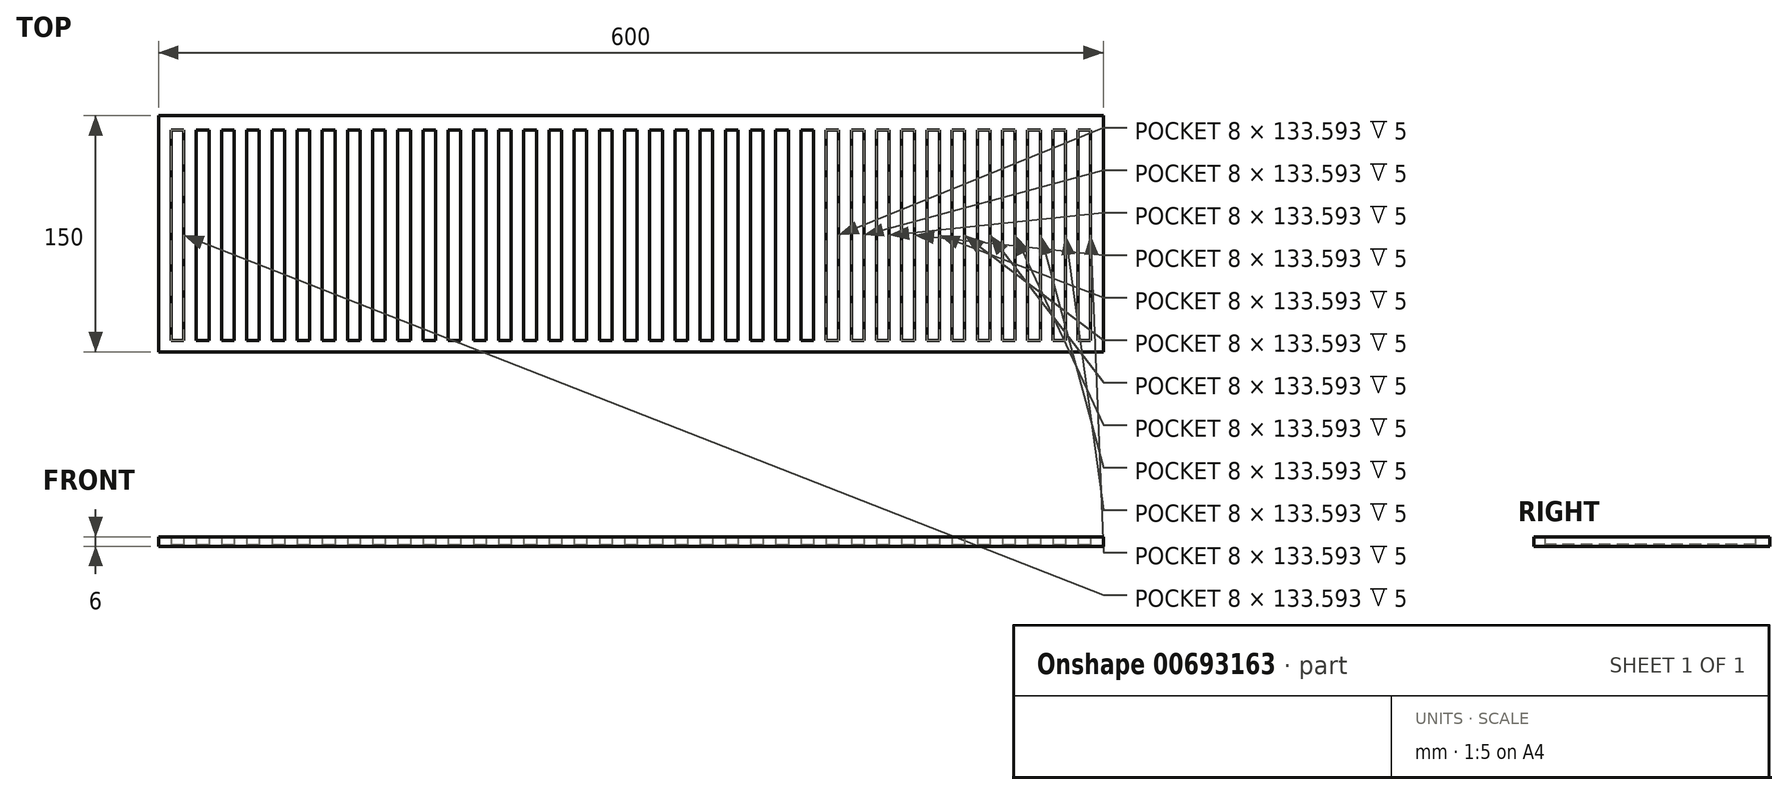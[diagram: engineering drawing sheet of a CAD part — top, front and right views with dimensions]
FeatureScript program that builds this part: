
annotation { "Feature Type Name" : "Feature", "Feature Type Description" : "" }
export const myFeature = defineFeature(function(context is Context, id is Id, definition is map)
    precondition{}
    {
        {
            var Q0;
            Q0=qCreatedBy(makeId("Top.planeOp"),FACE);
            var sketch = newSketch(context, id + "F0", { "sketchPlane" : qUnion([Q0])});
            skLineSegment(sketch, "E0.bottom", {"start": v(-288.8, 29.5) * mm, "end": v(311.2, 29.5) * mm});
            skLineSegment(sketch, "E0.top", {"start": v(-288.8, -120.5) * mm, "end": v(311.2, -120.5) * mm});
            skLineSegment(sketch, "E0.left", {"start": v(-288.8, 29.5) * mm, "end": v(-288.8, -120.5) * mm});
            skLineSegment(sketch, "E0.right", {"start": v(311.2, 29.5) * mm, "end": v(311.2, -120.5) * mm});
            skLineSegment(sketch, "E1.bottom", {"start": v(-280.8, 20.35) * mm, "end": v(-272.8, 20.35) * mm});
            skLineSegment(sketch, "E1.top", {"start": v(-280.8, -113.25) * mm, "end": v(-272.8, -113.25) * mm});
            skLineSegment(sketch, "E1.left", {"start": v(-280.8, 20.35) * mm, "end": v(-280.8, -113.25) * mm});
            skLineSegment(sketch, "E1.right", {"start": v(-272.8, 20.35) * mm, "end": v(-272.8, -113.25) * mm});
            skLineSegment(sketch, "E2.1.0.0", {"start": v(-264.8, 20.35) * mm, "end": v(-256.8, 20.35) * mm});
            skLineSegment(sketch, "E2.1.0.1", {"start": v(-264.8, 20.35) * mm, "end": v(-264.8, -113.25) * mm});
            skLineSegment(sketch, "E2.1.0.2", {"start": v(-256.8, 20.35) * mm, "end": v(-256.8, -113.25) * mm});
            skLineSegment(sketch, "E2.1.0.3", {"start": v(-264.8, -113.25) * mm, "end": v(-256.8, -113.25) * mm});
            skLineSegment(sketch, "E2.2.0.0", {"start": v(-248.8, 20.35) * mm, "end": v(-240.8, 20.35) * mm});
            skLineSegment(sketch, "E2.2.0.1", {"start": v(-248.8, 20.35) * mm, "end": v(-248.8, -113.25) * mm});
            skLineSegment(sketch, "E2.2.0.2", {"start": v(-240.8, 20.35) * mm, "end": v(-240.8, -113.25) * mm});
            skLineSegment(sketch, "E2.2.0.3", {"start": v(-248.8, -113.25) * mm, "end": v(-240.8, -113.25) * mm});
            skLineSegment(sketch, "E2.3.0.0", {"start": v(-232.8, 20.35) * mm, "end": v(-224.8, 20.35) * mm});
            skLineSegment(sketch, "E2.3.0.1", {"start": v(-232.8, 20.35) * mm, "end": v(-232.8, -113.25) * mm});
            skLineSegment(sketch, "E2.3.0.2", {"start": v(-224.8, 20.35) * mm, "end": v(-224.8, -113.25) * mm});
            skLineSegment(sketch, "E2.3.0.3", {"start": v(-232.8, -113.25) * mm, "end": v(-224.8, -113.25) * mm});
            skLineSegment(sketch, "E2.4.0.0", {"start": v(-216.8, 20.35) * mm, "end": v(-208.8, 20.35) * mm});
            skLineSegment(sketch, "E2.4.0.1", {"start": v(-216.8, 20.35) * mm, "end": v(-216.8, -113.25) * mm});
            skLineSegment(sketch, "E2.4.0.2", {"start": v(-208.8, 20.35) * mm, "end": v(-208.8, -113.25) * mm});
            skLineSegment(sketch, "E2.4.0.3", {"start": v(-216.8, -113.25) * mm, "end": v(-208.8, -113.25) * mm});
            skLineSegment(sketch, "E2.5.0.0", {"start": v(-200.8, 20.35) * mm, "end": v(-192.8, 20.35) * mm});
            skLineSegment(sketch, "E2.5.0.1", {"start": v(-200.8, 20.35) * mm, "end": v(-200.8, -113.25) * mm});
            skLineSegment(sketch, "E2.5.0.2", {"start": v(-192.8, 20.35) * mm, "end": v(-192.8, -113.25) * mm});
            skLineSegment(sketch, "E2.5.0.3", {"start": v(-200.8, -113.25) * mm, "end": v(-192.8, -113.25) * mm});
            skLineSegment(sketch, "E2.6.0.0", {"start": v(-184.8, 20.35) * mm, "end": v(-176.8, 20.35) * mm});
            skLineSegment(sketch, "E2.6.0.1", {"start": v(-184.8, 20.35) * mm, "end": v(-184.8, -113.25) * mm});
            skLineSegment(sketch, "E2.6.0.2", {"start": v(-176.8, 20.35) * mm, "end": v(-176.8, -113.25) * mm});
            skLineSegment(sketch, "E2.6.0.3", {"start": v(-184.8, -113.25) * mm, "end": v(-176.8, -113.25) * mm});
            skLineSegment(sketch, "E2.7.0.0", {"start": v(-168.8, 20.35) * mm, "end": v(-160.8, 20.35) * mm});
            skLineSegment(sketch, "E2.7.0.1", {"start": v(-168.8, 20.35) * mm, "end": v(-168.8, -113.25) * mm});
            skLineSegment(sketch, "E2.7.0.2", {"start": v(-160.8, 20.35) * mm, "end": v(-160.8, -113.25) * mm});
            skLineSegment(sketch, "E2.7.0.3", {"start": v(-168.8, -113.25) * mm, "end": v(-160.8, -113.25) * mm});
            skLineSegment(sketch, "E2.8.0.0", {"start": v(-152.8, 20.35) * mm, "end": v(-144.8, 20.35) * mm});
            skLineSegment(sketch, "E2.8.0.1", {"start": v(-152.8, 20.35) * mm, "end": v(-152.8, -113.25) * mm});
            skLineSegment(sketch, "E2.8.0.2", {"start": v(-144.8, 20.35) * mm, "end": v(-144.8, -113.25) * mm});
            skLineSegment(sketch, "E2.8.0.3", {"start": v(-152.8, -113.25) * mm, "end": v(-144.8, -113.25) * mm});
            skLineSegment(sketch, "E2.9.0.0", {"start": v(-136.8, 20.35) * mm, "end": v(-128.8, 20.35) * mm});
            skLineSegment(sketch, "E2.9.0.1", {"start": v(-136.8, 20.35) * mm, "end": v(-136.8, -113.25) * mm});
            skLineSegment(sketch, "E2.9.0.2", {"start": v(-128.8, 20.35) * mm, "end": v(-128.8, -113.25) * mm});
            skLineSegment(sketch, "E2.9.0.3", {"start": v(-136.8, -113.25) * mm, "end": v(-128.8, -113.25) * mm});
            skLineSegment(sketch, "E2.10.0.0", {"start": v(-120.8, 20.35) * mm, "end": v(-112.8, 20.35) * mm});
            skLineSegment(sketch, "E2.10.0.1", {"start": v(-120.8, 20.35) * mm, "end": v(-120.8, -113.25) * mm});
            skLineSegment(sketch, "E2.10.0.2", {"start": v(-112.8, 20.35) * mm, "end": v(-112.8, -113.25) * mm});
            skLineSegment(sketch, "E2.10.0.3", {"start": v(-120.8, -113.25) * mm, "end": v(-112.8, -113.25) * mm});
            skLineSegment(sketch, "E2.11.0.0", {"start": v(-104.8, 20.35) * mm, "end": v(-96.8, 20.35) * mm});
            skLineSegment(sketch, "E2.11.0.1", {"start": v(-104.8, 20.35) * mm, "end": v(-104.8, -113.25) * mm});
            skLineSegment(sketch, "E2.11.0.2", {"start": v(-96.8, 20.35) * mm, "end": v(-96.8, -113.25) * mm});
            skLineSegment(sketch, "E2.11.0.3", {"start": v(-104.8, -113.25) * mm, "end": v(-96.8, -113.25) * mm});
            skLineSegment(sketch, "E2.12.0.0", {"start": v(-88.8, 20.35) * mm, "end": v(-80.8, 20.35) * mm});
            skLineSegment(sketch, "E2.12.0.1", {"start": v(-88.8, 20.35) * mm, "end": v(-88.8, -113.25) * mm});
            skLineSegment(sketch, "E2.12.0.2", {"start": v(-80.8, 20.35) * mm, "end": v(-80.8, -113.25) * mm});
            skLineSegment(sketch, "E2.12.0.3", {"start": v(-88.8, -113.25) * mm, "end": v(-80.8, -113.25) * mm});
            skLineSegment(sketch, "E2.13.0.0", {"start": v(-72.8, 20.35) * mm, "end": v(-64.8, 20.35) * mm});
            skLineSegment(sketch, "E2.13.0.1", {"start": v(-72.8, 20.35) * mm, "end": v(-72.8, -113.25) * mm});
            skLineSegment(sketch, "E2.13.0.2", {"start": v(-64.8, 20.35) * mm, "end": v(-64.8, -113.25) * mm});
            skLineSegment(sketch, "E2.13.0.3", {"start": v(-72.8, -113.25) * mm, "end": v(-64.8, -113.25) * mm});
            skLineSegment(sketch, "E2.14.0.0", {"start": v(-56.8, 20.35) * mm, "end": v(-48.8, 20.35) * mm});
            skLineSegment(sketch, "E2.14.0.1", {"start": v(-56.8, 20.35) * mm, "end": v(-56.8, -113.25) * mm});
            skLineSegment(sketch, "E2.14.0.2", {"start": v(-48.8, 20.35) * mm, "end": v(-48.8, -113.25) * mm});
            skLineSegment(sketch, "E2.14.0.3", {"start": v(-56.8, -113.25) * mm, "end": v(-48.8, -113.25) * mm});
            skLineSegment(sketch, "E2.15.0.0", {"start": v(-40.8, 20.35) * mm, "end": v(-32.8, 20.35) * mm});
            skLineSegment(sketch, "E2.15.0.1", {"start": v(-40.8, 20.35) * mm, "end": v(-40.8, -113.25) * mm});
            skLineSegment(sketch, "E2.15.0.2", {"start": v(-32.8, 20.35) * mm, "end": v(-32.8, -113.25) * mm});
            skLineSegment(sketch, "E2.15.0.3", {"start": v(-40.8, -113.25) * mm, "end": v(-32.8, -113.25) * mm});
            skLineSegment(sketch, "E2.16.0.0", {"start": v(-24.8, 20.35) * mm, "end": v(-16.8, 20.35) * mm});
            skLineSegment(sketch, "E2.16.0.1", {"start": v(-24.8, 20.35) * mm, "end": v(-24.8, -113.25) * mm});
            skLineSegment(sketch, "E2.16.0.2", {"start": v(-16.8, 20.35) * mm, "end": v(-16.8, -113.25) * mm});
            skLineSegment(sketch, "E2.16.0.3", {"start": v(-24.8, -113.25) * mm, "end": v(-16.8, -113.25) * mm});
            skLineSegment(sketch, "E2.17.0.0", {"start": v(-8.8, 20.35) * mm, "end": v(-0.8, 20.35) * mm});
            skLineSegment(sketch, "E2.17.0.1", {"start": v(-8.8, 20.35) * mm, "end": v(-8.8, -113.25) * mm});
            skLineSegment(sketch, "E2.17.0.2", {"start": v(-0.8, 20.35) * mm, "end": v(-0.8, -113.25) * mm});
            skLineSegment(sketch, "E2.17.0.3", {"start": v(-8.8, -113.25) * mm, "end": v(-0.8, -113.25) * mm});
            skLineSegment(sketch, "E2.18.0.0", {"start": v(7.2, 20.35) * mm, "end": v(15.2, 20.35) * mm});
            skLineSegment(sketch, "E2.18.0.1", {"start": v(7.2, 20.35) * mm, "end": v(7.2, -113.25) * mm});
            skLineSegment(sketch, "E2.18.0.2", {"start": v(15.2, 20.35) * mm, "end": v(15.2, -113.25) * mm});
            skLineSegment(sketch, "E2.18.0.3", {"start": v(7.2, -113.25) * mm, "end": v(15.2, -113.25) * mm});
            skLineSegment(sketch, "E2.19.0.0", {"start": v(23.2, 20.35) * mm, "end": v(31.2, 20.35) * mm});
            skLineSegment(sketch, "E2.19.0.1", {"start": v(23.2, 20.35) * mm, "end": v(23.2, -113.25) * mm});
            skLineSegment(sketch, "E2.19.0.2", {"start": v(31.2, 20.35) * mm, "end": v(31.2, -113.25) * mm});
            skLineSegment(sketch, "E2.19.0.3", {"start": v(23.2, -113.25) * mm, "end": v(31.2, -113.25) * mm});
            skLineSegment(sketch, "E2.20.0.0", {"start": v(39.2, 20.35) * mm, "end": v(47.2, 20.35) * mm});
            skLineSegment(sketch, "E2.20.0.1", {"start": v(39.2, 20.35) * mm, "end": v(39.2, -113.25) * mm});
            skLineSegment(sketch, "E2.20.0.2", {"start": v(47.2, 20.35) * mm, "end": v(47.2, -113.25) * mm});
            skLineSegment(sketch, "E2.20.0.3", {"start": v(39.2, -113.25) * mm, "end": v(47.2, -113.25) * mm});
            skLineSegment(sketch, "E2.21.0.0", {"start": v(55.2, 20.35) * mm, "end": v(63.2, 20.35) * mm});
            skLineSegment(sketch, "E2.21.0.1", {"start": v(55.2, 20.35) * mm, "end": v(55.2, -113.25) * mm});
            skLineSegment(sketch, "E2.21.0.2", {"start": v(63.2, 20.35) * mm, "end": v(63.2, -113.25) * mm});
            skLineSegment(sketch, "E2.21.0.3", {"start": v(55.2, -113.25) * mm, "end": v(63.2, -113.25) * mm});
            skLineSegment(sketch, "E2.22.0.0", {"start": v(71.2, 20.35) * mm, "end": v(79.2, 20.35) * mm});
            skLineSegment(sketch, "E2.22.0.1", {"start": v(71.2, 20.35) * mm, "end": v(71.2, -113.25) * mm});
            skLineSegment(sketch, "E2.22.0.2", {"start": v(79.2, 20.35) * mm, "end": v(79.2, -113.25) * mm});
            skLineSegment(sketch, "E2.22.0.3", {"start": v(71.2, -113.25) * mm, "end": v(79.2, -113.25) * mm});
            skLineSegment(sketch, "E2.23.0.0", {"start": v(87.2, 20.35) * mm, "end": v(95.2, 20.35) * mm});
            skLineSegment(sketch, "E2.23.0.1", {"start": v(87.2, 20.35) * mm, "end": v(87.2, -113.25) * mm});
            skLineSegment(sketch, "E2.23.0.2", {"start": v(95.2, 20.35) * mm, "end": v(95.2, -113.25) * mm});
            skLineSegment(sketch, "E2.23.0.3", {"start": v(87.2, -113.25) * mm, "end": v(95.2, -113.25) * mm});
            skLineSegment(sketch, "E2.24.0.0", {"start": v(103.2, 20.35) * mm, "end": v(111.2, 20.35) * mm});
            skLineSegment(sketch, "E2.24.0.1", {"start": v(103.2, 20.35) * mm, "end": v(103.2, -113.25) * mm});
            skLineSegment(sketch, "E2.24.0.2", {"start": v(111.2, 20.35) * mm, "end": v(111.2, -113.25) * mm});
            skLineSegment(sketch, "E2.24.0.3", {"start": v(103.2, -113.25) * mm, "end": v(111.2, -113.25) * mm});
            skLineSegment(sketch, "E2.25.0.0", {"start": v(119.2, 20.35) * mm, "end": v(127.2, 20.35) * mm});
            skLineSegment(sketch, "E2.25.0.1", {"start": v(119.2, 20.35) * mm, "end": v(119.2, -113.25) * mm});
            skLineSegment(sketch, "E2.25.0.2", {"start": v(127.2, 20.35) * mm, "end": v(127.2, -113.25) * mm});
            skLineSegment(sketch, "E2.25.0.3", {"start": v(119.2, -113.25) * mm, "end": v(127.2, -113.25) * mm});
            skLineSegment(sketch, "E2.26.0.0", {"start": v(135.2, 20.35) * mm, "end": v(143.2, 20.35) * mm});
            skLineSegment(sketch, "E2.26.0.1", {"start": v(135.2, 20.35) * mm, "end": v(135.2, -113.25) * mm});
            skLineSegment(sketch, "E2.26.0.2", {"start": v(143.2, 20.35) * mm, "end": v(143.2, -113.25) * mm});
            skLineSegment(sketch, "E2.26.0.3", {"start": v(135.2, -113.25) * mm, "end": v(143.2, -113.25) * mm});
            skLineSegment(sketch, "E2.27.0.0", {"start": v(151.2, 20.35) * mm, "end": v(159.2, 20.35) * mm});
            skLineSegment(sketch, "E2.27.0.1", {"start": v(151.2, 20.35) * mm, "end": v(151.2, -113.25) * mm});
            skLineSegment(sketch, "E2.27.0.2", {"start": v(159.2, 20.35) * mm, "end": v(159.2, -113.25) * mm});
            skLineSegment(sketch, "E2.27.0.3", {"start": v(151.2, -113.25) * mm, "end": v(159.2, -113.25) * mm});
            skLineSegment(sketch, "E2.28.0.0", {"start": v(167.2, 20.35) * mm, "end": v(175.2, 20.35) * mm});
            skLineSegment(sketch, "E2.28.0.1", {"start": v(167.2, 20.35) * mm, "end": v(167.2, -113.25) * mm});
            skLineSegment(sketch, "E2.28.0.2", {"start": v(175.2, 20.35) * mm, "end": v(175.2, -113.25) * mm});
            skLineSegment(sketch, "E2.28.0.3", {"start": v(167.2, -113.25) * mm, "end": v(175.2, -113.25) * mm});
            skLineSegment(sketch, "E2.29.0.0", {"start": v(183.2, 20.35) * mm, "end": v(191.2, 20.35) * mm});
            skLineSegment(sketch, "E2.29.0.1", {"start": v(183.2, 20.35) * mm, "end": v(183.2, -113.25) * mm});
            skLineSegment(sketch, "E2.29.0.2", {"start": v(191.2, 20.35) * mm, "end": v(191.2, -113.25) * mm});
            skLineSegment(sketch, "E2.29.0.3", {"start": v(183.2, -113.25) * mm, "end": v(191.2, -113.25) * mm});
            skLineSegment(sketch, "E2.30.0.0", {"start": v(199.2, 20.35) * mm, "end": v(207.2, 20.35) * mm});
            skLineSegment(sketch, "E2.30.0.1", {"start": v(199.2, 20.35) * mm, "end": v(199.2, -113.25) * mm});
            skLineSegment(sketch, "E2.30.0.2", {"start": v(207.2, 20.35) * mm, "end": v(207.2, -113.25) * mm});
            skLineSegment(sketch, "E2.30.0.3", {"start": v(199.2, -113.25) * mm, "end": v(207.2, -113.25) * mm});
            skLineSegment(sketch, "E2.31.0.0", {"start": v(215.2, 20.35) * mm, "end": v(223.2, 20.35) * mm});
            skLineSegment(sketch, "E2.31.0.1", {"start": v(215.2, 20.35) * mm, "end": v(215.2, -113.25) * mm});
            skLineSegment(sketch, "E2.31.0.2", {"start": v(223.2, 20.35) * mm, "end": v(223.2, -113.25) * mm});
            skLineSegment(sketch, "E2.31.0.3", {"start": v(215.2, -113.25) * mm, "end": v(223.2, -113.25) * mm});
            skLineSegment(sketch, "E2.32.0.0", {"start": v(231.2, 20.35) * mm, "end": v(239.2, 20.35) * mm});
            skLineSegment(sketch, "E2.32.0.1", {"start": v(231.2, 20.35) * mm, "end": v(231.2, -113.25) * mm});
            skLineSegment(sketch, "E2.32.0.2", {"start": v(239.2, 20.35) * mm, "end": v(239.2, -113.25) * mm});
            skLineSegment(sketch, "E2.32.0.3", {"start": v(231.2, -113.25) * mm, "end": v(239.2, -113.25) * mm});
            skLineSegment(sketch, "E2.33.0.0", {"start": v(247.2, 20.35) * mm, "end": v(255.2, 20.35) * mm});
            skLineSegment(sketch, "E2.33.0.1", {"start": v(247.2, 20.35) * mm, "end": v(247.2, -113.25) * mm});
            skLineSegment(sketch, "E2.33.0.2", {"start": v(255.2, 20.35) * mm, "end": v(255.2, -113.25) * mm});
            skLineSegment(sketch, "E2.33.0.3", {"start": v(247.2, -113.25) * mm, "end": v(255.2, -113.25) * mm});
            skLineSegment(sketch, "E2.34.0.0", {"start": v(263.2, 20.35) * mm, "end": v(271.2, 20.35) * mm});
            skLineSegment(sketch, "E2.34.0.1", {"start": v(263.2, 20.35) * mm, "end": v(263.2, -113.25) * mm});
            skLineSegment(sketch, "E2.34.0.2", {"start": v(271.2, 20.35) * mm, "end": v(271.2, -113.25) * mm});
            skLineSegment(sketch, "E2.34.0.3", {"start": v(263.2, -113.25) * mm, "end": v(271.2, -113.25) * mm});
            skLineSegment(sketch, "E2.35.0.0", {"start": v(279.2, 20.35) * mm, "end": v(287.2, 20.35) * mm});
            skLineSegment(sketch, "E2.35.0.1", {"start": v(279.2, 20.35) * mm, "end": v(279.2, -113.25) * mm});
            skLineSegment(sketch, "E2.35.0.2", {"start": v(287.2, 20.35) * mm, "end": v(287.2, -113.25) * mm});
            skLineSegment(sketch, "E2.35.0.3", {"start": v(279.2, -113.25) * mm, "end": v(287.2, -113.25) * mm});
            skLineSegment(sketch, "E2.36.0.0", {"start": v(295.2, 20.35) * mm, "end": v(303.2, 20.35) * mm});
            skLineSegment(sketch, "E2.36.0.1", {"start": v(295.2, 20.35) * mm, "end": v(295.2, -113.25) * mm});
            skLineSegment(sketch, "E2.36.0.2", {"start": v(303.2, 20.35) * mm, "end": v(303.2, -113.25) * mm});
            skLineSegment(sketch, "E2.36.0.3", {"start": v(295.2, -113.25) * mm, "end": v(303.2, -113.25) * mm});
            skLineSegment(sketch, "E2.direction1", {"start": v(-280.8, 20.35) * mm, "end": v(-264.8, 20.35) * mm, "construction": true});
            skSolve(sketch);
        }
        {
            var Q0;
            Q0=qSketchRegion(id+"F0",true);
            extrude(context, id + "F1", {"entities" : qUnion([Q0]), "depth" : 5 * mm, "offsetDistance" : 25 * mm});
        }
        {
            var Q0;
            Q0=makeQuery(id+"F1.opExtrude","CAP_FACE",FACE,{"disambiguationData":[OSD([sQuery(id+"F0.wireOp",EDGE,"E0.bottom"),sQuery(id+"F0.wireOp",EDGE,"E0.top"),sQuery(id+"F0.wireOp",EDGE,"E0.left"),sQuery(id+"F0.wireOp",EDGE,"E0.right"),sQuery(id+"F0.wireOp",EDGE,"Q3saARHD-Gs58-2NVK-PtzY-fhxvJSEAU8xS.bottom"),sQuery(id+"F0.wireOp",EDGE,"Q3saARHD-Gs58-2NVK-PtzY-fhxvJSEAU8xS.top"),sQuery(id+"F0.wireOp",EDGE,"Q3saARHD-Gs58-2NVK-PtzY-fhxvJSEAU8xS.left"),sQuery(id+"F0.wireOp",EDGE,"Q3saARHD-Gs58-2NVK-PtzY-fhxvJSEAU8xS.right"),sQuery(id+"F0.wireOp",EDGE,"dcdc5563-4537-49a2-8787-ece9258b1a45.0.1.0"),sQuery(id+"F0.wireOp",EDGE,"dcdc5563-4537-49a2-8787-ece9258b1a45.0.1.1"),sQuery(id+"F0.wireOp",EDGE,"dcdc5563-4537-49a2-8787-ece9258b1a45.0.1.2"),sQuery(id+"F0.wireOp",EDGE,"dcdc5563-4537-49a2-8787-ece9258b1a45.0.1.3"),sQuery(id+"F0.wireOp",EDGE,"dcdc5563-4537-49a2-8787-ece9258b1a45.0.2.0"),sQuery(id+"F0.wireOp",EDGE,"dcdc5563-4537-49a2-8787-ece9258b1a45.0.2.1"),sQuery(id+"F0.wireOp",EDGE,"dcdc5563-4537-49a2-8787-ece9258b1a45.0.2.2"),sQuery(id+"F0.wireOp",EDGE,"dcdc5563-4537-49a2-8787-ece9258b1a45.0.2.3"),sQuery(id+"F0.wireOp",EDGE,"dcdc5563-4537-49a2-8787-ece9258b1a45.0.3.0"),sQuery(id+"F0.wireOp",EDGE,"dcdc5563-4537-49a2-8787-ece9258b1a45.0.3.1"),sQuery(id+"F0.wireOp",EDGE,"dcdc5563-4537-49a2-8787-ece9258b1a45.0.3.2"),sQuery(id+"F0.wireOp",EDGE,"dcdc5563-4537-49a2-8787-ece9258b1a45.0.3.3"),sQuery(id+"F0.wireOp",EDGE,"dcdc5563-4537-49a2-8787-ece9258b1a45.0.4.0"),sQuery(id+"F0.wireOp",EDGE,"dcdc5563-4537-49a2-8787-ece9258b1a45.0.4.1"),sQuery(id+"F0.wireOp",EDGE,"dcdc5563-4537-49a2-8787-ece9258b1a45.0.4.2"),sQuery(id+"F0.wireOp",EDGE,"dcdc5563-4537-49a2-8787-ece9258b1a45.0.4.3"),sQuery(id+"F0.wireOp",EDGE,"dcdc5563-4537-49a2-8787-ece9258b1a45.0.5.0"),sQuery(id+"F0.wireOp",EDGE,"dcdc5563-4537-49a2-8787-ece9258b1a45.0.5.1"),sQuery(id+"F0.wireOp",EDGE,"dcdc5563-4537-49a2-8787-ece9258b1a45.0.5.2"),sQuery(id+"F0.wireOp",EDGE,"dcdc5563-4537-49a2-8787-ece9258b1a45.0.5.3"),sQuery(id+"F0.wireOp",EDGE,"dcdc5563-4537-49a2-8787-ece9258b1a45.0.6.0"),sQuery(id+"F0.wireOp",EDGE,"dcdc5563-4537-49a2-8787-ece9258b1a45.0.6.1"),sQuery(id+"F0.wireOp",EDGE,"dcdc5563-4537-49a2-8787-ece9258b1a45.0.6.2"),sQuery(id+"F0.wireOp",EDGE,"dcdc5563-4537-49a2-8787-ece9258b1a45.0.6.3")])],"isStart":true});
            var sketch = newSketch(context, id + "F2", { "sketchPlane" : qUnion([Q0])});
            skLineSegment(sketch, "E3.bottom", {"start": v(-288.8, -29.5) * mm, "end": v(311.2, -29.5) * mm});
            skLineSegment(sketch, "E3.top", {"start": v(-288.8, 120.5) * mm, "end": v(311.2, 120.5) * mm});
            skLineSegment(sketch, "E3.left", {"start": v(-288.8, -29.5) * mm, "end": v(-288.8, 120.5) * mm});
            skLineSegment(sketch, "E3.right", {"start": v(311.2, -29.5) * mm, "end": v(311.2, 120.5) * mm});
            skSolve(sketch);
        }
        {
            var Q0;
            Q0=qSketchRegion(id+"F2",true);
            extrude(context, id + "F3", {"entities" : qUnion([Q0]), "operationType" : NewBodyOperationType.ADD, "depth" : 1 * mm, "offsetDistance" : 25 * mm});
        }
    });
